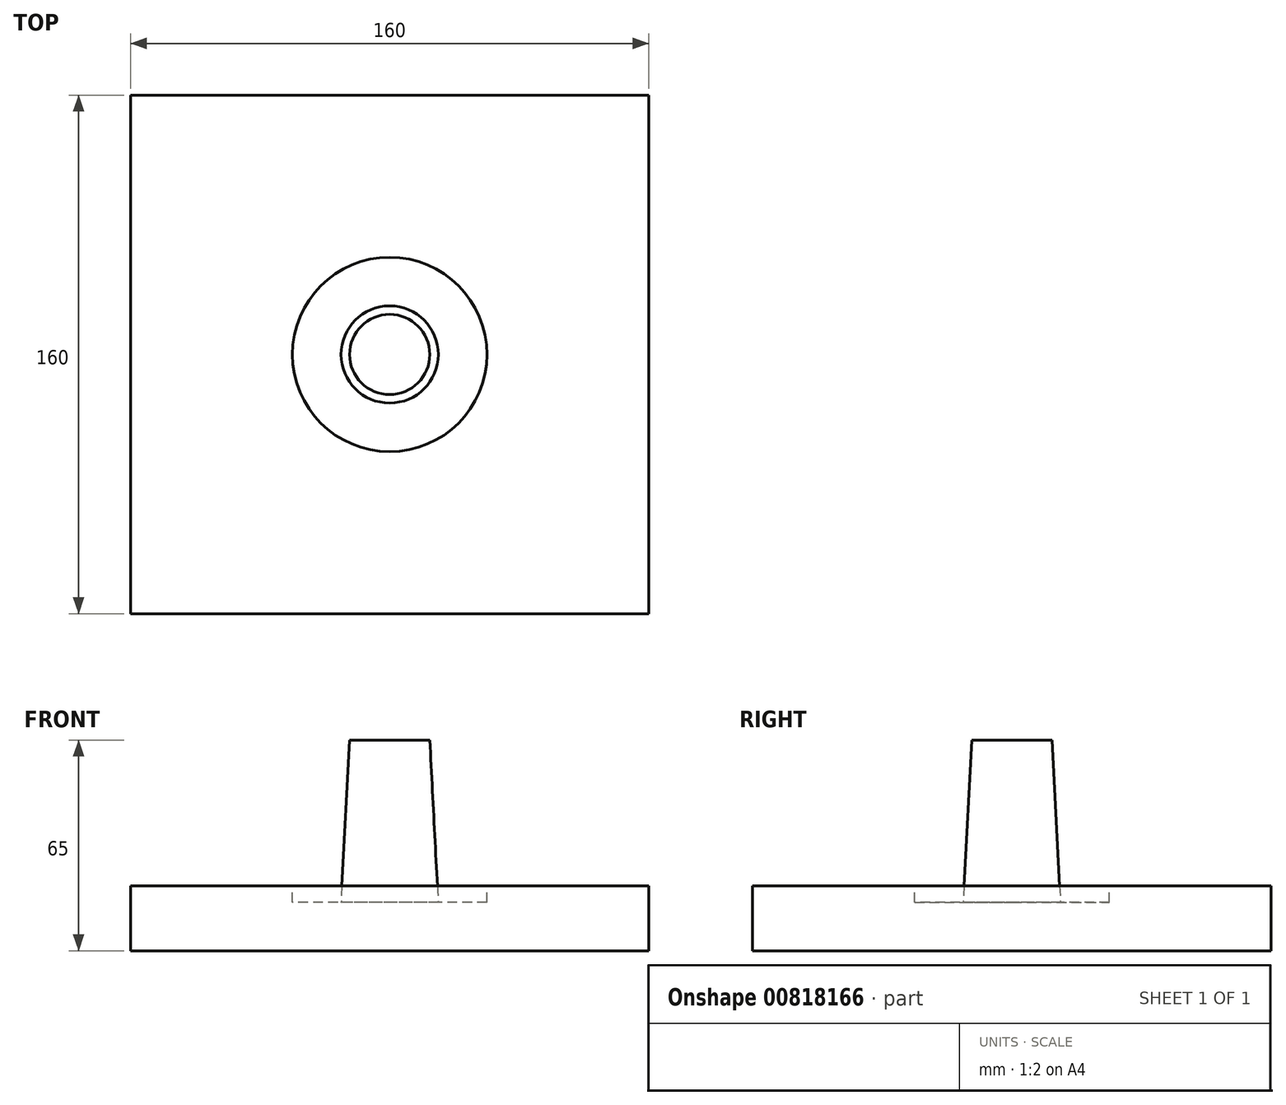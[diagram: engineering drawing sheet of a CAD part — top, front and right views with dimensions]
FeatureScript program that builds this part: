
annotation { "Feature Type Name" : "Feature", "Feature Type Description" : "" }
export const myFeature = defineFeature(function(context is Context, id is Id, definition is map)
    precondition{}
    {
        {
            var Q0;
            Q0=qCreatedBy(makeId("Top.planeOp"),FACE);
            var sketch = newSketch(context, id + "F0", { "sketchPlane" : qUnion([Q0])});
            skLineSegment(sketch, "E0.bottom", {"start": v(0, 0) * mm, "end": v(160, 0) * mm});
            skLineSegment(sketch, "E0.top", {"start": v(0, 160) * mm, "end": v(160, 160) * mm});
            skLineSegment(sketch, "E0.left", {"start": v(0, 0) * mm, "end": v(0, 160) * mm});
            skLineSegment(sketch, "E0.right", {"start": v(160, 0) * mm, "end": v(160, 160) * mm});
            skSolve(sketch);
        }
        {
            var Q0;
            Q0 = qSketchRegion(id + "F0", true);
            extrude(context, id + "F1", {"entities" : qUnion([Q0]), "depth" : 20 * mm, "offsetDistance" : 25 * mm});
        }
        {
            var Q0;
            Q0=makeQuery(id+"F1.opExtrude","CAP_FACE",FACE,{"disambiguationData":[OSD([sQuery(id+"F0.wireOp",EDGE,"E0.bottom"),sQuery(id+"F0.wireOp",EDGE,"E0.top"),sQuery(id+"F0.wireOp",EDGE,"E0.left"),sQuery(id+"F0.wireOp",EDGE,"E0.right")])],"isStart":false});
            var sketch = newSketch(context, id + "F2", { "sketchPlane" : qUnion([Q0])});
            skCircle(sketch, "E1", {"center": v(80, 80) * mm, "radius": 30 * mm});
            skLineSegment(sketch, "E2", {"start": v(160, 0) * mm, "end": v(0, 160) * mm, "construction": true});
            skLineSegment(sketch, "E3", {"start": v(0, 0) * mm, "end": v(160, 160) * mm, "construction": true});
            skSolve(sketch);
        }
        {
            var Q0;
            Q0=makeQuery(id+"F2.imprint","IMPRINT",FACE,{"disambiguationData":[TD([[makeQuery(id+"F2.imprint","IMPRINT",EDGE,{"derivedFrom":sQuery(id+"F2.wireOp",EDGE,"E1")}),1.0]])]});
            extrude(context, id + "F3", {"entities" : qUnion([Q0]), "operationType" : NewBodyOperationType.REMOVE, "oppositeDirection" : true, "depth" : 5 * mm, "offsetDistance" : 25 * mm});
        }
        {
            var Q0;
            Q0=makeQuery(id+"F3.boolean.opBoolean","COPY",FACE,{"derivedFrom":makeQuery(id+"F3.opExtrude","CAP_FACE",FACE,{"disambiguationData":[OSD([sQuery(id+"F2.wireOp",EDGE,"E1")])],"isStart":false})});
            var sketch = newSketch(context, id + "F4", { "sketchPlane" : qUnion([Q0])});
            skCircle(sketch, "E4", {"center": v(80, 80) * mm, "radius": 15 * mm});
            skSolve(sketch);
        }
        {
            var Q0;
            Q0=makeQuery(id+"F4.imprint","IMPRINT",FACE,{"disambiguationData":[TD([[makeQuery(id+"F4.imprint","IMPRINT",EDGE,{"derivedFrom":sQuery(id+"F4.wireOp",EDGE,"E4")}),1.0]])]});
            extrude(context, id + "F5", {"entities" : qUnion([Q0]), "depth" : 50 * mm, "offsetDistance" : 25 * mm, "hasDraft" : true, "draftAngle" : 3 * degree, "draftPullDirection" : true});
        }
    });
